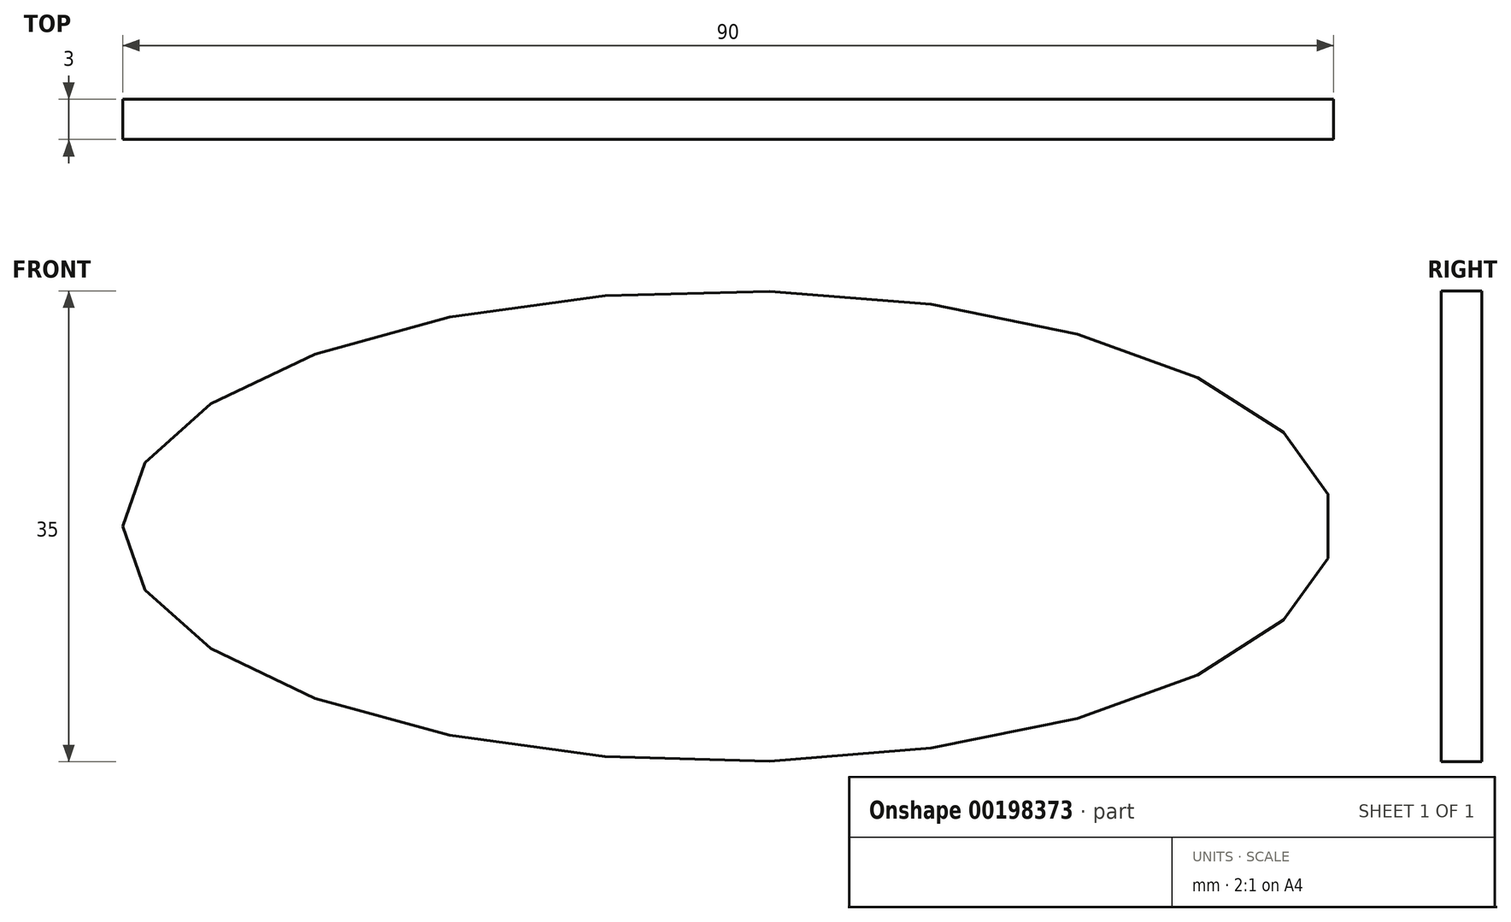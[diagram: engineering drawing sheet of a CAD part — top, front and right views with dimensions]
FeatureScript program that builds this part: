
annotation { "Feature Type Name" : "Feature", "Feature Type Description" : "" }
export const myFeature = defineFeature(function(context is Context, id is Id, definition is map)
    precondition{}
    {
        {
            var Q0;
            Q0=qCreatedBy(makeId("Front.planeOp"),FACE);
            var sketch = newSketch(context, id + "F0", { "sketchPlane" : qUnion([Q0])});
            skEllipse(sketch, "E0", {"center": v(-9.7, -46.2) * mm, "majorRadius": 45 * mm, "minorRadius": 17.5 * mm, "majorAxis": v(-1, 0)});
            skSolve(sketch);
        }
        {
            var Q0;
            Q0 = qSketchRegion(id + "F0", true);
            extrude(context, id + "F1", {"entities" : qUnion([Q0]), "depth" : 3 * mm});
        }
    });
